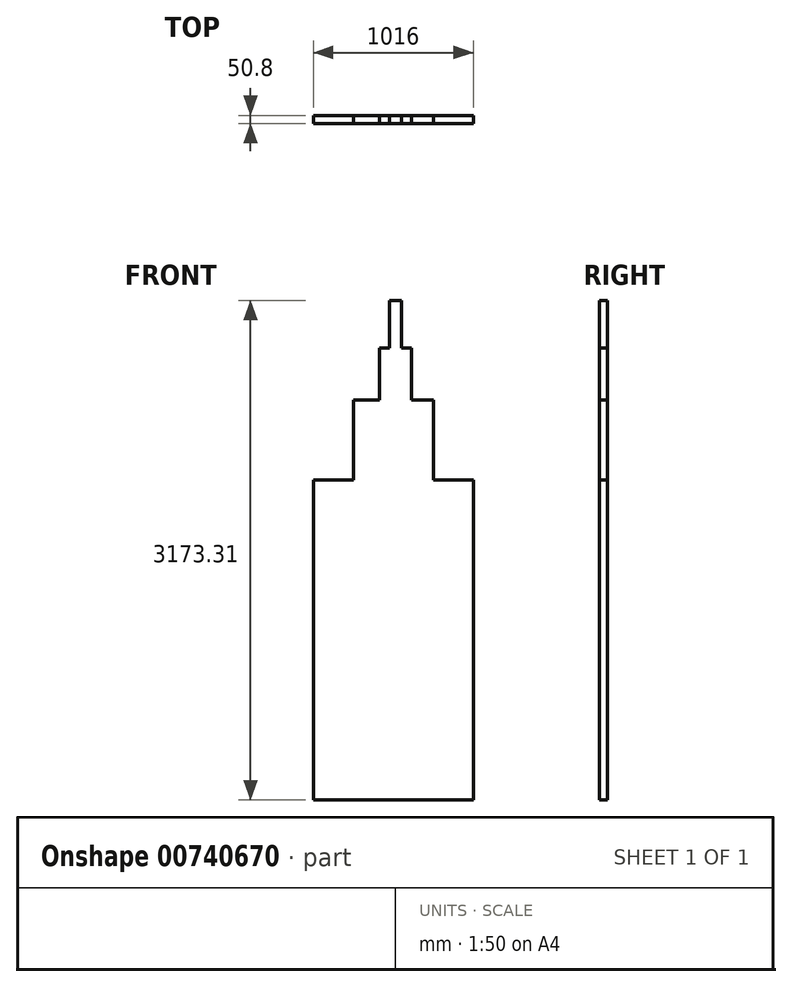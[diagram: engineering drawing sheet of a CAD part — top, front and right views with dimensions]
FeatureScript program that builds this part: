
annotation { "Feature Type Name" : "Feature", "Feature Type Description" : "" }
export const myFeature = defineFeature(function(context is Context, id is Id, definition is map)
    precondition{}
    {
        {
            var Q0;
            Q0=qCreatedBy(makeId("Front.planeOp"),FACE);
            var sketch = newSketch(context, id + "F0", { "sketchPlane" : qUnion([Q0])});
            skLineSegment(sketch, "E0.bottom", {"start": v(-7244.44, 4834) * mm, "end": v(375.56, 4834) * mm, "construction": true});
            skLineSegment(sketch, "E0.top", {"start": v(-7244.44, -246) * mm, "end": v(375.56, -246) * mm, "construction": true});
            skLineSegment(sketch, "E0.left", {"start": v(-7244.44, 4834) * mm, "end": v(-7244.44, -246) * mm, "construction": true});
            skLineSegment(sketch, "E0.right", {"start": v(375.56, 4834) * mm, "end": v(375.56, -246) * mm, "construction": true});
            skLineSegment(sketch, "E1", {"start": v(-5956.55, 918.7) * mm, "end": v(-5956.55, 2950.7) * mm});
            skLineSegment(sketch, "E2", {"start": v(-5956.55, 918.7) * mm, "end": v(-4940.55, 918.7) * mm});
            skLineSegment(sketch, "E3", {"start": v(-4940.55, 2950.7) * mm, "end": v(-5194.55, 2950.7) * mm});
            skLineSegment(sketch, "E4", {"start": v(-5956.55, 2950.7) * mm, "end": v(-5702.55, 2950.7) * mm});
            skLineSegment(sketch, "E5", {"start": v(-5702.55, 2950.7) * mm, "end": v(-5702.55, 3458.7) * mm});
            skLineSegment(sketch, "E6", {"start": v(-5194.55, 2950.7) * mm, "end": v(-5194.55, 3458.7) * mm});
            skLineSegment(sketch, "E7", {"start": v(-5702.55, 3458.7) * mm, "end": v(-5536.38, 3458.7) * mm});
            skLineSegment(sketch, "E8", {"start": v(-5194.55, 3458.7) * mm, "end": v(-5332.3, 3458.7) * mm});
            skLineSegment(sketch, "E9", {"start": v(-5536.38, 3458.7) * mm, "end": v(-5536.38, 3788.9) * mm});
            skLineSegment(sketch, "E10", {"start": v(-5332.3, 3458.7) * mm, "end": v(-5332.3, 3788.9) * mm});
            skLineSegment(sketch, "E11", {"start": v(-5536.38, 3788.9) * mm, "end": v(-5473.08, 3788.9) * mm});
            skLineSegment(sketch, "E12", {"start": v(-5332.3, 3788.9) * mm, "end": v(-5396.27, 3788.9) * mm});
            skLineSegment(sketch, "E13", {"start": v(-5396.27, 3788.9) * mm, "end": v(-5396.27, 4092) * mm});
            skLineSegment(sketch, "E14", {"start": v(-5396.27, 4092) * mm, "end": v(-5468.43, 4092) * mm});
            skLineSegment(sketch, "E15", {"start": v(-5473.08, 3788.9) * mm, "end": v(-5473.08, 4092) * mm});
            skLineSegment(sketch, "E16", {"start": v(-5468.43, 4092) * mm, "end": v(-5473.08, 4092) * mm});
            skLineSegment(sketch, "E17.MirrorCS", {"start": v(-3528.77, 4092) * mm, "end": v(-3524.12, 4092) * mm});
            skLineSegment(sketch, "E18.MirrorCS", {"start": v(-3600.92, 4092) * mm, "end": v(-3528.77, 4092) * mm});
            skLineSegment(sketch, "E19.MirrorCS", {"start": v(-3664.9, 3788.9) * mm, "end": v(-3600.92, 3788.9) * mm});
            skLineSegment(sketch, "E20.MirrorCS", {"start": v(-3460.82, 3788.9) * mm, "end": v(-3524.12, 3788.9) * mm});
            skLineSegment(sketch, "E21.MirrorCS", {"start": v(-3600.92, 3788.9) * mm, "end": v(-3600.92, 4092) * mm});
            skLineSegment(sketch, "E22.MirrorCS", {"start": v(-3294.65, 3458.7) * mm, "end": v(-3460.82, 3458.7) * mm});
            skLineSegment(sketch, "E23.MirrorCS", {"start": v(-3524.12, 3788.9) * mm, "end": v(-3524.12, 4092) * mm});
            skLineSegment(sketch, "E24.MirrorCS", {"start": v(-3460.82, 3458.7) * mm, "end": v(-3460.82, 3788.9) * mm});
            skLineSegment(sketch, "E25.MirrorCS", {"start": v(-3664.9, 3458.7) * mm, "end": v(-3664.9, 3788.9) * mm});
            skLineSegment(sketch, "E26.MirrorCS", {"start": v(-3802.65, 3458.7) * mm, "end": v(-3664.9, 3458.7) * mm});
            skLineSegment(sketch, "E27.MirrorCS", {"start": v(-3040.65, 2950.7) * mm, "end": v(-3294.65, 2950.7) * mm});
            skLineSegment(sketch, "E28.MirrorCS", {"start": v(-4056.65, 2950.7) * mm, "end": v(-3802.65, 2950.7) * mm});
            skLineSegment(sketch, "E29.MirrorCS", {"start": v(-3294.65, 2950.7) * mm, "end": v(-3294.65, 3458.7) * mm});
            skLineSegment(sketch, "E30.MirrorCS", {"start": v(-3802.65, 2950.7) * mm, "end": v(-3802.65, 3458.7) * mm});
            skLineSegment(sketch, "E31.MirrorCS", {"start": v(-3040.65, 918.7) * mm, "end": v(-4056.65, 918.7) * mm});
            skLineSegment(sketch, "E32.MirrorCS", {"start": v(-3040.65, 918.7) * mm, "end": v(-3040.65, 2950.7) * mm});
            skLineSegment(sketch, "E33", {"start": v(-4940.55, 2471.26) * mm, "end": v(-4056.65, 2471.26) * mm});
            skLineSegment(sketch, "E34", {"start": v(-4940.55, 1934.7) * mm, "end": v(-4056.65, 1934.7) * mm});
            skLineSegment(sketch, "E35", {"start": v(-4940.55, 2950.7) * mm, "end": v(-4940.55, 2471.26) * mm});
            skLineSegment(sketch, "E36", {"start": v(-4940.55, 1934.7) * mm, "end": v(-4940.55, 918.7) * mm});
            skLineSegment(sketch, "E37", {"start": v(-4056.65, 2950.7) * mm, "end": v(-4056.65, 2471.26) * mm});
            skLineSegment(sketch, "E38", {"start": v(-4056.65, 1934.7) * mm, "end": v(-4056.65, 918.7) * mm});
            skLineSegment(sketch, "E39", {"start": v(-4940.55, 2471.26) * mm, "end": v(-4940.55, 1934.7) * mm});
            skLineSegment(sketch, "E40", {"start": v(-4056.65, 2471.26) * mm, "end": v(-4056.65, 1934.7) * mm});
            skSolve(sketch);
        }
        {
            var Q0;
            Q0=makeQuery(id+"F0.imprint","IMPRINT",FACE,{"disambiguationData":[TD([[makeQuery(id+"F0.imprint","IMPRINT",EDGE,{"derivedFrom":sQuery(id+"F0.wireOp",EDGE,"E1")}),-1.0]])]});
            extrude(context, id + "F1", {"entities" : qUnion([Q0]), "depth" : 50.8 * mm, "offsetDistance" : 25.4 * mm});
        }
        {
            var Q0;
            Q0=makeQuery(id+"F0.imprint","IMPRINT",FACE,{"disambiguationData":[TD([[makeQuery(id+"F0.imprint","IMPRINT",EDGE,{"derivedFrom":sQuery(id+"F0.wireOp",EDGE,"E1")}),-1.0]])]});
            extrude(context, id + "F2", {"entities" : qUnion([Q0]), "operationType" : NewBodyOperationType.ADD, "depth" : 50.8 * mm, "offsetDistance" : 25.4 * mm});
        }
    });
